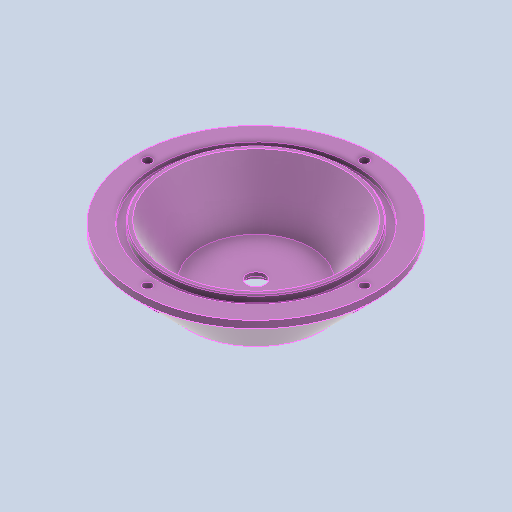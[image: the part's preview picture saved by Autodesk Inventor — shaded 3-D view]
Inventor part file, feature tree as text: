
AUTODESK INVENTOR PART (.ipt)
format: ipt  version: 2023 (Build 270158000, 158)  size: 241,664 bytes
history: native  units: mm
features: sketch x3, revolve x1, plane x1, hole x1, extrude x1, pattern_circular x1, chamfer x1
ambient origin geometry x8: Origin, YZ Plane, XZ Plane, XY Plane, X Axis, Y Axis, Z Axis, Center Point
bodies: Solid1 (feature_tree)
feature tree (9):
  revolve  "Revolution1"  [1 undecoded]
  plane  "Work Plane1"
  hole  "Hole1"  [1 undecoded]
  extrude  "Extrusion2"  Depth=10.0mm
  pattern_circular  "Circular Pattern1"  Count=5  [1 undecoded]
  chamfer  "Chamfer1"  Distance=1.23mm
  sketch  "Sketch1"  dims[d0=5.0mm d1=3.0mm]
  sketch  "Sketch2"  dims[d10=90.0deg d11=2.0mm]
  sketch  "Sketch4"  dims[d12=2.0mm d20=17.0mm d23=50.0mm d24=1.23mm d25=2.0mm d26=30.0mm d28=65.0mm d31=2.4mm d32=6.0mm d33=4.5mm d34=6.0mm d35=90.0deg d36=50.0mm d37=0.0mm d38=29.5mm d39=40.0mm d40=360.0deg d43=5.585054mm d45=-8.0mm d49=10.0mm d50=0.0mm d51=16.3mm d52=2.0mm d53=135.0deg d54=0.3mm d55=2.0mm d56=45.0deg]
note: 3 required parameter values undecoded (feature->parameter linkage not recoverable at this tier; creation-order binding heuristic only, values carry confidence <= 0.55)